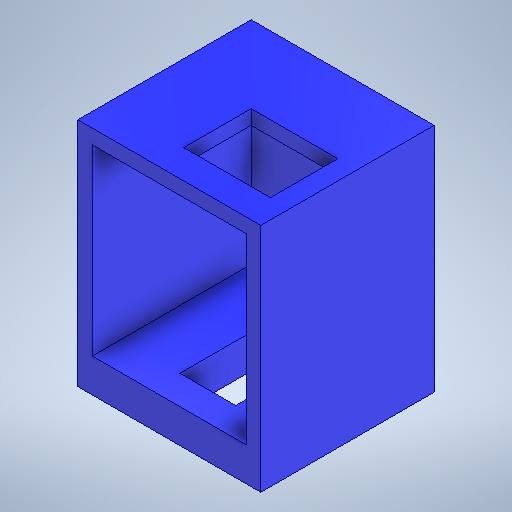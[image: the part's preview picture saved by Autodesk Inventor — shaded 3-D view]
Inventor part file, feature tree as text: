
AUTODESK INVENTOR PART (.ipt)
format: ipt  version: 2025.2 (Build 292293000, 293)  size: 404,992 bytes
history: native  units: mm
features: extrude x5, sketch x5, projected_geometry x4, other x1
ambient origin geometry x8: Origin, YZ Plane, XZ Plane, XY Plane, X Axis, Y Axis, Z Axis, Center Point
bodies: Body1 (feature_tree)
feature tree (15):
  other  "Těleso1"
  extrude  "Vysunutí1"  Depth=21.0mm
  extrude  "Vysunutí2"  Depth=26.0mm
  extrude  "Vysunutí3"  Depth=18.0mm TaperAngle=0.0deg
  extrude  "Vysunutí4"  Depth=3.5mm
  extrude  "Vysunutí6"  Depth=16.5mm TaperAngle=0.0deg
  sketch  "Náčrt1"
  sketch  "Náčrt4"
  projected_geometry  "Promítnutá smyčka2"
  sketch  "Náčrt5"
  projected_geometry  "Promítnutá smyčka3"
  sketch  "Náčrt6"
  projected_geometry  "Promítnutá smyčka4"
  sketch  "Náčrt8"
  projected_geometry  "Promítnutá smyčka6"
